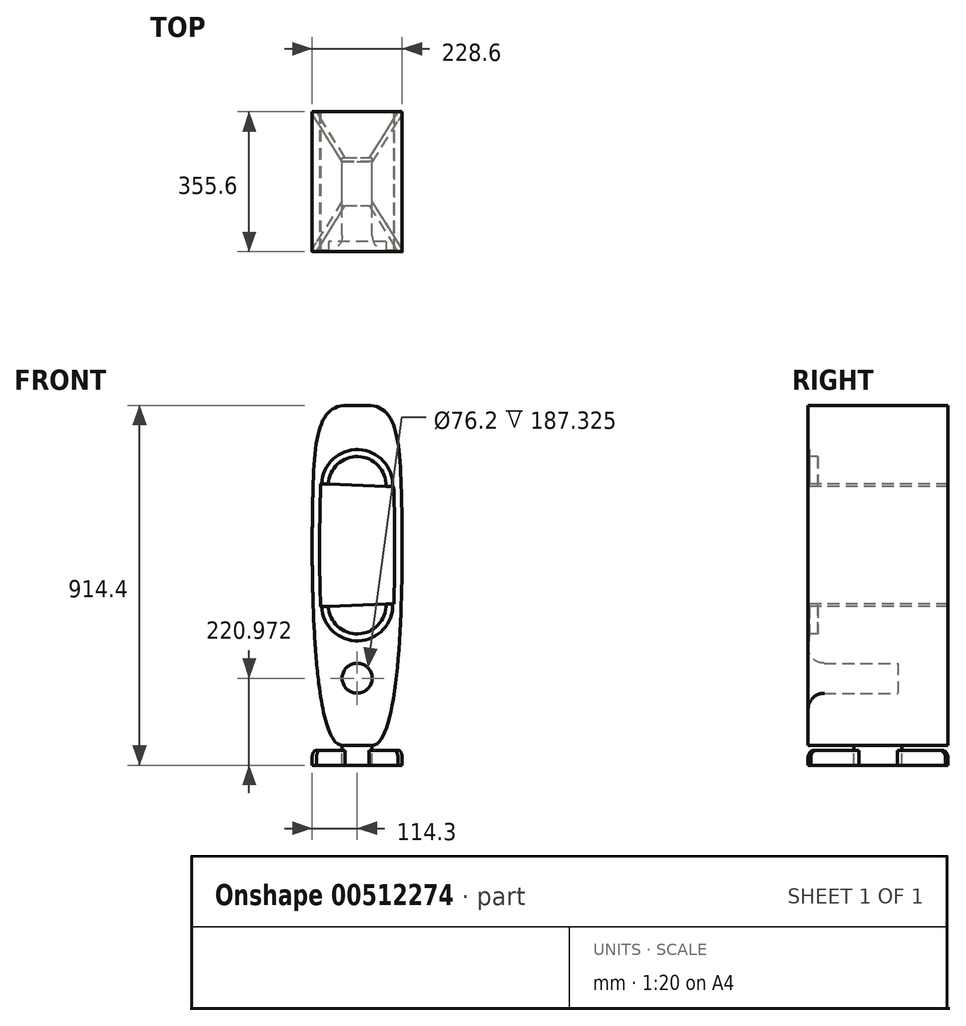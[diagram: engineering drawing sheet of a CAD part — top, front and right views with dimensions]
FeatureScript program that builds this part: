
annotation { "Feature Type Name" : "Feature", "Feature Type Description" : "" }
export const myFeature = defineFeature(function(context is Context, id is Id, definition is map)
    precondition{}
    {
        {
            var Q0;
            Q0=qCreatedBy(makeId("Front.planeOp"),FACE);
            var sketch = newSketch(context, id + "F0", { "sketchPlane" : qUnion([Q0])});
            skCircle(sketch, "E0", {"center": v(0, 152.4) * mm, "radius": 90.49 * mm});
            skCircle(sketch, "E1", {"center": v(0, 152.4) * mm, "radius": 73.03 * mm});
            skCircle(sketch, "E2", {"center": v(0, -152.4) * mm, "radius": 90.49 * mm});
            skCircle(sketch, "E3", {"center": v(0, -152.4) * mm, "radius": 73.03 * mm});
            skCircle(sketch, "E4", {"center": v(33.34, 0) * mm, "radius": 52.39 * mm});
            skCircle(sketch, "E5", {"center": v(33.34, 0) * mm, "radius": 38.1 * mm});
            skSolve(sketch);
        }
        {
            var Q0;
            Q0=qCreatedBy(makeId("Front.planeOp"),FACE);
            var sketch = newSketch(context, id + "F1", { "sketchPlane" : qUnion([Q0])});
            skLineSegment(sketch, "E6", {"start": v(-25.4, 355.6) * mm, "end": v(25.4, 355.6) * mm});
            skLineSegment(sketch, "E7", {"start": v(-38.1, -508) * mm, "end": v(38.1, -508) * mm});
            skFitSpline(sketch, "E8", {"points": [v(-25.4, 355.6) * mm, v(-112.46, 131.94) * mm, v(-38.1, -508) * mm], "startDerivative": vector(-581.78, 0) * mm, "endDerivative": vector(351.6, 0) * mm});
            skFitSpline(sketch, "E9", {"points": [v(25.4, 355.6) * mm, v(112.46, 131.94) * mm, v(38.1, -508) * mm], "startDerivative": vector(581.78, 0) * mm, "endDerivative": vector(-351.6, 0) * mm});
            skLineSegment(sketch, "E10", {"start": v(-114.3, 34.49) * mm, "end": v(-114.3, -81.25) * mm});
            skLineSegment(sketch, "E11", {"start": v(-111.69, 156.4) * mm, "end": v(-119.91, -73.49) * mm});
            skLineSegment(sketch, "E12", {"start": v(-111.69, 156.4) * mm, "end": v(0, 152.4) * mm});
            skLineSegment(sketch, "E13", {"start": v(0, -152.4) * mm, "end": v(-111.69, -156.4) * mm});
            skLineSegment(sketch, "E14", {"start": v(-111.64, -157.68) * mm, "end": v(-111.69, -156.4) * mm});
            skLineSegment(sketch, "E15", {"start": v(0, 152.4) * mm, "end": v(4258.77, 0) * mm});
            skLineSegment(sketch, "E16", {"start": v(4258.77, 0) * mm, "end": v(0, -152.4) * mm});
            skCircle(sketch, "E17", {"center": v(0, -337.83) * mm, "radius": 79.38 * mm});
            skLineSegment(sketch, "E18", {"start": v(0, -337.83) * mm, "end": v(-97.66, -350.04) * mm});
            skLineSegment(sketch, "E19", {"start": v(-97.66, -350.04) * mm, "end": v(-163.56, 177.1) * mm});
            skCircle(sketch, "E20", {"center": v(0, -337.83) * mm, "radius": 38.1 * mm});
            skFitSpline(sketch, "E21.0", {"points": [v(25.4, 336.55) * mm, v(27.86, 336.55) * mm, v(32.48, 336.33) * mm, v(38.57, 335.4) * mm, v(43.91, 333.96) * mm, v(48.62, 332.05) * mm, v(52.86, 329.66) * mm, v(56.78, 326.73) * mm, v(60.49, 323.17) * mm, v(64.04, 318.87) * mm, v(67.45, 313.74) * mm, v(70.68, 307.73) * mm, v(73.71, 300.82) * mm, v(77.46, 290.41) * mm, v(81.54, 275.18) * mm, v(85.44, 253.53) * mm, v(88.41, 228.7) * mm, v(90.6, 200.8) * mm, v(92.19, 170) * mm, v(93.14, 141.98) * mm, v(93.78, 118.21) * mm, v(94.35, 93.64) * mm, v(94.9, 61.54) * mm, v(95.25, 21.27) * mm, v(95.29, -34.17) * mm, v(94.4, -105.65) * mm, v(92.04, -177.05) * mm, v(89.1, -232.35) * mm, v(86.35, -272.46) * mm, v(83, -310.75) * mm, v(79.04, -346.75) * mm, v(74.43, -380) * mm, v(69.16, -409.99) * mm, v(64.21, -431.83) * mm, v(59.96, -447.12) * mm, v(56.63, -457.4) * mm, v(53.22, -466.41) * mm, v(49.76, -474.04) * mm, v(46.36, -480.18) * mm, v(43.7, -483.94) * mm, v(41.84, -486.11) * mm, v(40.61, -487.33) * mm, v(39.6, -488.16) * mm, v(38.85, -488.65) * mm, v(38.39, -488.88) * mm, v(38.18, -488.94) * mm, v(38.14, -488.95) * mm, v(38.13, -488.95) * mm, v(38.1, -488.95) * mm]});
            skLineSegment(sketch, "E21.1", {"start": v(-25.4, 336.55) * mm, "end": v(25.4, 336.55) * mm});
            skFitSpline(sketch, "E21.2", {"points": [v(-25.4, 336.55) * mm, v(-27.86, 336.55) * mm, v(-32.48, 336.33) * mm, v(-38.57, 335.4) * mm, v(-43.91, 333.96) * mm, v(-48.62, 332.05) * mm, v(-52.86, 329.66) * mm, v(-56.78, 326.73) * mm, v(-60.49, 323.17) * mm, v(-64.04, 318.87) * mm, v(-67.45, 313.74) * mm, v(-70.68, 307.73) * mm, v(-73.71, 300.82) * mm, v(-77.46, 290.41) * mm, v(-81.54, 275.18) * mm, v(-85.44, 253.53) * mm, v(-88.41, 228.7) * mm, v(-90.6, 200.8) * mm, v(-92.19, 170) * mm, v(-93.14, 141.98) * mm, v(-93.78, 118.21) * mm, v(-94.35, 93.64) * mm, v(-94.9, 61.54) * mm, v(-95.25, 21.27) * mm, v(-95.29, -34.17) * mm, v(-94.4, -105.65) * mm, v(-92.04, -177.05) * mm, v(-89.1, -232.35) * mm, v(-86.35, -272.46) * mm, v(-83, -310.75) * mm, v(-79.04, -346.75) * mm, v(-74.43, -380) * mm, v(-69.16, -409.99) * mm, v(-64.21, -431.83) * mm, v(-59.96, -447.12) * mm, v(-56.63, -457.4) * mm, v(-53.22, -466.41) * mm, v(-49.76, -474.04) * mm, v(-46.36, -480.18) * mm, v(-43.7, -483.94) * mm, v(-41.84, -486.11) * mm, v(-40.61, -487.33) * mm, v(-39.6, -488.16) * mm, v(-38.85, -488.65) * mm, v(-38.39, -488.88) * mm, v(-38.18, -488.94) * mm, v(-38.14, -488.95) * mm, v(-38.13, -488.95) * mm, v(-38.1, -488.95) * mm]});
            skLineSegment(sketch, "E21.3", {"start": v(-38.1, -488.95) * mm, "end": v(38.1, -488.95) * mm});
            skPoint(sketch, "E22", {"position": v(0, -299.73) * mm});
            skPoint(sketch, "E23", {"position": v(0, -258.45) * mm});
            skLineSegment(sketch, "E24", {"start": v(-95, 47.62) * mm, "end": v(95, 47.62) * mm});
            skLineSegment(sketch, "E25", {"start": v(-94.77, 66.67) * mm, "end": v(94.77, 66.67) * mm});
            skLineSegment(sketch, "E26", {"start": v(-94.82, -66.67) * mm, "end": v(94.82, -66.67) * mm});
            skLineSegment(sketch, "E27", {"start": v(-95.04, -47.62) * mm, "end": v(95.04, -47.62) * mm});
            skLineSegment(sketch, "E28", {"start": v(253.42, 57.15) * mm, "end": v(318.07, 57.15) * mm});
            skLineSegment(sketch, "E29", {"start": v(253.7, 61.91) * mm, "end": v(300.48, 61.91) * mm});
            skLineSegment(sketch, "E30", {"start": v(255.73, 52.39) * mm, "end": v(319.23, 52.39) * mm});
            skLineSegment(sketch, "E31", {"start": v(259.21, -61.91) * mm, "end": v(326.14, -61.91) * mm});
            skLineSegment(sketch, "E32", {"start": v(240.79, -57.15) * mm, "end": v(315.43, -57.15) * mm});
            skLineSegment(sketch, "E33", {"start": v(242.27, -52.39) * mm, "end": v(300.37, -52.39) * mm});
            skLineSegment(sketch, "E34", {"start": v(-89.03, -231.78) * mm, "end": v(89.03, -231.78) * mm});
            skLineSegment(sketch, "E35", {"start": v(-87.8, -250.83) * mm, "end": v(87.8, -250.83) * mm});
            skLineSegment(sketch, "E36", {"start": v(-74.37, -379.1) * mm, "end": v(74.37, -379.1) * mm});
            skLineSegment(sketch, "E37", {"start": v(-71.17, -398.15) * mm, "end": v(71.17, -398.15) * mm});
            skLineSegment(sketch, "E38", {"start": v(-85.6, 250.83) * mm, "end": v(85.6, 250.83) * mm});
            skLineSegment(sketch, "E39", {"start": v(-87.92, 231.78) * mm, "end": v(87.92, 231.78) * mm});
            skPoint(sketch, "E40", {"position": v(-78.76, -347.67) * mm});
            skSolve(sketch);
        }
        {
            var Q0;
            Q0=qCreatedBy(makeId("Right.planeOp"),FACE);
            var sketch = newSketch(context, id + "F2", { "sketchPlane" : qUnion([Q0])});
            skLineSegment(sketch, "E41", {"start": v(-179.41, -337.83) * mm, "end": v(228.6, -337.83) * mm});
            skLineSegment(sketch, "E42", {"start": v(0, -337.83) * mm, "end": v(0, -258.45) * mm});
            skArc(sketch, "E43", {"start": v(0, -258.45) * mm, "mid": v(12.09, -287.64) * mm, "end": v(41.28, -299.73) * mm});
            skLineSegment(sketch, "E44", {"start": v(41.28, -299.73) * mm, "end": v(228.6, -299.73) * mm});
            skLineSegment(sketch, "E45", {"start": v(228.6, -299.73) * mm, "end": v(228.6, -337.83) * mm});
            skSolve(sketch);
        }
        {
            var Q0;
            {var subQ6=sQuery(id+"F1.wireOp",EDGE,"E6");Q0=makeQuery(id+"F1.imprint","IMPRINT",FACE,{"disambiguationData":[TD([[makeQuery(id+"F1.imprint","IMPRINT",EDGE,{"derivedFrom":subQ6}),-1.0]])]});}
            var Q1;
            {var subQ0=sQuery(id+"F1.wireOp",EDGE,"E21.1");Q1=makeQuery(id+"F1.imprint","IMPRINT",FACE,{"disambiguationData":[TD([[makeQuery(id+"F1.imprint","IMPRINT",EDGE,{"derivedFrom":subQ0}),-1.0]])]});}
            var Q2;
            {var subQ2=sQuery(id+"F1.wireOp",EDGE,"E15");var subQ4=sQuery(id+"F1.wireOp",EDGE,"E9");var subQ5=makeQuery(id+"F1.imprint","INTERSECT",VERTEX,{"derivedFrom":[subQ4,subQ2]});Q2=makeQuery(id+"F1.imprint","IMPRINT",FACE,{"disambiguationData":[TD([[makeQuery(id+"F1.imprint","IMPRINT",EDGE,{"disambiguationData":[TD([[subQ5,-1.0]])],"derivedFrom":subQ4}),-1.0]])]});}
            var Q3;
            {var subQ2=sQuery(id+"F1.wireOp",EDGE,"E12");var subQ4=sQuery(id+"F1.wireOp",EDGE,"E8");var subQ5=makeQuery(id+"F1.imprint","INTERSECT",VERTEX,{"derivedFrom":[subQ4,subQ2]});Q3=makeQuery(id+"F1.imprint","IMPRINT",FACE,{"disambiguationData":[TD([[makeQuery(id+"F1.imprint","IMPRINT",EDGE,{"disambiguationData":[TD([[subQ5,-1.0]])],"derivedFrom":subQ4}),1.0]])]});}
            var Q4;
            {var subQ0=sQuery(id+"F1.wireOp",EDGE,"E25");Q4=makeQuery(id+"F1.imprint","IMPRINT",FACE,{"disambiguationData":[TD([[makeQuery(id+"F1.imprint","IMPRINT",EDGE,{"derivedFrom":subQ0}),1.0]])]});}
            var Q5;
            {var subQ0=sQuery(id+"F1.wireOp",EDGE,"E24");Q5=makeQuery(id+"F1.imprint","IMPRINT",FACE,{"disambiguationData":[TD([[makeQuery(id+"F1.imprint","IMPRINT",EDGE,{"derivedFrom":subQ0}),1.0]])]});}
            var Q6;
            {var subQ0=sQuery(id+"F1.wireOp",EDGE,"E24");Q6=makeQuery(id+"F1.imprint","IMPRINT",FACE,{"disambiguationData":[TD([[makeQuery(id+"F1.imprint","IMPRINT",EDGE,{"derivedFrom":subQ0}),-1.0]])]});}
            var Q7;
            {var subQ0=sQuery(id+"F1.wireOp",EDGE,"E26");Q7=makeQuery(id+"F1.imprint","IMPRINT",FACE,{"disambiguationData":[TD([[makeQuery(id+"F1.imprint","IMPRINT",EDGE,{"derivedFrom":subQ0}),1.0]])]});}
            var Q8;
            {var subQ0=sQuery(id+"F1.wireOp",EDGE,"E26");Q8=makeQuery(id+"F1.imprint","IMPRINT",FACE,{"disambiguationData":[TD([[makeQuery(id+"F1.imprint","IMPRINT",EDGE,{"derivedFrom":subQ0}),-1.0]])]});}
            var Q9;
            Q9=makeQuery(id+"F1.imprint","IMPRINT",FACE,{"disambiguationData":[TD([[makeQuery(id+"F1.imprint","IMPRINT",EDGE,{"derivedFrom":sQuery(id+"F1.wireOp",EDGE,"E17")}),-1.0]])]});
            var Q10;
            {var subQ6=sQuery(id+"F1.wireOp",EDGE,"E7");Q10=makeQuery(id+"F1.imprint","IMPRINT",FACE,{"disambiguationData":[TD([[makeQuery(id+"F1.imprint","IMPRINT",EDGE,{"derivedFrom":subQ6}),1.0]])]});}
            var Q11;
            Q11=makeQuery(id+"F1.imprint","IMPRINT",FACE,{"disambiguationData":[TD([[makeQuery(id+"F1.imprint","IMPRINT",EDGE,{"derivedFrom":sQuery(id+"F1.wireOp",EDGE,"E17")}),1.0]])]});
            var Q12;
            {var subQ0=sQuery(id+"F1.wireOp",EDGE,"E13");var subQ1=sQuery(id+"F1.wireOp",EDGE,"E8");var subQ2=makeQuery(id+"F1.imprint","INTERSECT",VERTEX,{"derivedFrom":[subQ1,subQ0]});Q12=makeQuery(id+"F1.imprint","IMPRINT",FACE,{"disambiguationData":[TD([[makeQuery(id+"F1.imprint","IMPRINT",EDGE,{"disambiguationData":[TD([[subQ2,-1.0]])],"derivedFrom":subQ1}),1.0]])]});}
            var Q13;
            Q13=makeQuery(id+"F1.imprint","IMPRINT",FACE,{"disambiguationData":[TD([[makeQuery(id+"F1.imprint","IMPRINT",EDGE,{"derivedFrom":sQuery(id+"F1.wireOp",EDGE,"E20")}),1.0]])]});
            var Q14;
            {var subQ0=sQuery(id+"F1.wireOp",EDGE,"E39");Q14=makeQuery(id+"F1.imprint","IMPRINT",FACE,{"disambiguationData":[TD([[makeQuery(id+"F1.imprint","IMPRINT",EDGE,{"derivedFrom":subQ0}),-1.0]])]});}
            var Q15;
            {var subQ0=sQuery(id+"F1.wireOp",EDGE,"E38");Q15=makeQuery(id+"F1.imprint","IMPRINT",FACE,{"disambiguationData":[TD([[makeQuery(id+"F1.imprint","IMPRINT",EDGE,{"derivedFrom":subQ0}),-1.0]])]});}
            var Q16;
            {var subQ0=sQuery(id+"F1.wireOp",EDGE,"E34");Q16=makeQuery(id+"F1.imprint","IMPRINT",FACE,{"disambiguationData":[TD([[makeQuery(id+"F1.imprint","IMPRINT",EDGE,{"derivedFrom":subQ0}),1.0]])]});}
            var Q17;
            {var subQ0=sQuery(id+"F1.wireOp",EDGE,"E34");Q17=makeQuery(id+"F1.imprint","IMPRINT",FACE,{"disambiguationData":[TD([[makeQuery(id+"F1.imprint","IMPRINT",EDGE,{"derivedFrom":subQ0}),-1.0]])]});}
            var Q18;
            {var subQ0=sQuery(id+"F1.wireOp",EDGE,"E35");Q18=makeQuery(id+"F1.imprint","IMPRINT",FACE,{"disambiguationData":[TD([[makeQuery(id+"F1.imprint","IMPRINT",EDGE,{"derivedFrom":subQ0}),-1.0]])]});}
            var Q19;
            {var subQ0=sQuery(id+"F1.wireOp",EDGE,"E21.3");Q19=makeQuery(id+"F1.imprint","IMPRINT",FACE,{"disambiguationData":[TD([[makeQuery(id+"F1.imprint","IMPRINT",EDGE,{"derivedFrom":subQ0}),1.0]])]});}
            var Q20;
            {var subQ0=sQuery(id+"F1.wireOp",EDGE,"E36");var subQ1=sQuery(id+"F1.wireOp",EDGE,"E17");var subQ2=makeQuery(id+"F1.imprint","INTERSECT",VERTEX,{"disambiguationData":[OD(0.0)],"derivedFrom":[subQ1,subQ0]});Q20=makeQuery(id+"F1.imprint","IMPRINT",FACE,{"disambiguationData":[TD([[makeQuery(id+"F1.imprint","IMPRINT",EDGE,{"disambiguationData":[TD([[subQ2,-1.0]])],"derivedFrom":subQ1}),1.0]])]});}
            var Q21;
            {var subQ0=sQuery(id+"F1.wireOp",EDGE,"E36");var subQ3=sQuery(id+"F1.wireOp",EDGE,"E17");var subQ4=makeQuery(id+"F1.imprint","INTERSECT",VERTEX,{"disambiguationData":[OD(0.0)],"derivedFrom":[subQ3,subQ0]});Q21=makeQuery(id+"F1.imprint","IMPRINT",FACE,{"disambiguationData":[TD([[makeQuery(id+"F1.imprint","IMPRINT",EDGE,{"disambiguationData":[TD([[subQ4,-1.0]])],"derivedFrom":subQ3}),-1.0]])]});}
            var Q22;
            {var subQ0=sQuery(id+"F1.wireOp",EDGE,"E37");var subQ1=sQuery(id+"F1.wireOp",EDGE,"E17");var subQ2=makeQuery(id+"F1.imprint","INTERSECT",VERTEX,{"disambiguationData":[OD(0.0)],"derivedFrom":[subQ1,subQ0]});Q22=makeQuery(id+"F1.imprint","IMPRINT",FACE,{"disambiguationData":[TD([[makeQuery(id+"F1.imprint","IMPRINT",EDGE,{"disambiguationData":[TD([[subQ2,-1.0]])],"derivedFrom":subQ1}),1.0]])]});}
            var Q23;
            {var subQ0=sQuery(id+"F1.wireOp",EDGE,"E37");var subQ1=sQuery(id+"F1.wireOp",EDGE,"E17");var subQ2=makeQuery(id+"F1.imprint","INTERSECT",VERTEX,{"disambiguationData":[OD(1.0)],"derivedFrom":[subQ1,subQ0]});Q23=makeQuery(id+"F1.imprint","IMPRINT",FACE,{"disambiguationData":[TD([[makeQuery(id+"F1.imprint","IMPRINT",EDGE,{"disambiguationData":[TD([[subQ2,-1.0]])],"derivedFrom":subQ1}),-1.0]])]});}
            extrude(context, id + "F3", {"entities" : qUnion([Q0, Q1, Q2, Q3, Q4, Q5, Q6, Q7, Q8, Q9, Q10, Q11, Q12, Q13, Q14, Q15, Q16, Q17, Q18, Q19, Q20, Q21, Q22, Q23]), "oppositeDirection" : true, "depth" : 355.6 * mm});
        }
        {
            var Q0;
            Q0=makeQuery(id+"F0.imprint","IMPRINT",FACE,{"disambiguationData":[TD([[makeQuery(id+"F0.imprint","IMPRINT",EDGE,{"derivedFrom":sQuery(id+"F0.wireOp",EDGE,"E0")}),1.0]])]});
            var Q1;
            Q1=makeQuery(id+"F0.imprint","IMPRINT",FACE,{"disambiguationData":[TD([[makeQuery(id+"F0.imprint","IMPRINT",EDGE,{"derivedFrom":sQuery(id+"F0.wireOp",EDGE,"E4")}),1.0]])]});
            var Q2;
            Q2=makeQuery(id+"F0.imprint","IMPRINT",FACE,{"disambiguationData":[TD([[makeQuery(id+"F0.imprint","IMPRINT",EDGE,{"derivedFrom":sQuery(id+"F0.wireOp",EDGE,"E2")}),1.0]])]});
            extrude(context, id + "F4", {"entities" : qUnion([Q0, Q1, Q2]), "operationType" : NewBodyOperationType.REMOVE, "oppositeDirection" : true, "depth" : 3.17 * mm});
        }
        {
            var Q0;
            Q0=makeQuery(id+"F0.imprint","IMPRINT",FACE,{"disambiguationData":[TD([[makeQuery(id+"F0.imprint","IMPRINT",EDGE,{"derivedFrom":sQuery(id+"F0.wireOp",EDGE,"E1")}),1.0]])]});
            var Q1;
            Q1=makeQuery(id+"F0.imprint","IMPRINT",FACE,{"disambiguationData":[TD([[makeQuery(id+"F0.imprint","IMPRINT",EDGE,{"derivedFrom":sQuery(id+"F0.wireOp",EDGE,"E5")}),1.0]])]});
            var Q2;
            Q2=makeQuery(id+"F0.imprint","IMPRINT",FACE,{"disambiguationData":[TD([[makeQuery(id+"F0.imprint","IMPRINT",EDGE,{"derivedFrom":sQuery(id+"F0.wireOp",EDGE,"E3")}),1.0]])]});
            extrude(context, id + "F5", {"entities" : qUnion([Q0, Q1, Q2]), "operationType" : NewBodyOperationType.REMOVE, "oppositeDirection" : true, "depth" : 25.4 * mm});
        }
        {
            var Q0;
            Q0=qSketchRegion(id+"F2",true);
            var Q1;
            Q1=sQuery(id+"F2.wireOp",EDGE,"E41");
            revolve(context, id + "F6", {"operationType" : NewBodyOperationType.REMOVE, "entities" : qUnion([Q0]), "axis" : qUnion([Q1]), "revolveType" : RevolveType.FULL, "oppositeDirection" : true});
        }
        {
            var Q0;
            Q0=makeQuery(id+"F3.opExtrude","CAP_EDGE",EDGE,{"disambiguationData":[OSD([sQuery(id+"F1.wireOp",EDGE,"E7")])],"isStart":true});
            cPoint(context, id + "F7", {"entities" : qUnion([Q0]), "parameter" : 0.5});
        }
        {
            var Q0;
            Q0=qCreatedBy(makeId("Top.planeOp"),FACE);
            var Q1;
            Q1=qCreatedBy(id+"F7",VERTEX);
            cPlane(context, id + "F8", {"entities" : qUnion([Q0, Q1]), "cplaneType" : CPlaneType.PLANE_POINT, "offset" : 25.4 * mm, "width" : 152.4 * mm, "height" : 152.4 * mm});
        }
        {
            var Q0;
            Q0=qCreatedBy(id+"F8.planeOp",FACE);
            var sketch = newSketch(context, id + "F9", { "sketchPlane" : qUnion([Q0])});
            skLineSegment(sketch, "E46.bottom", {"start": v(-114.3, 0) * mm, "end": v(114.3, 0) * mm});
            skLineSegment(sketch, "E46.top", {"start": v(-114.3, 355.6) * mm, "end": v(114.3, 355.6) * mm});
            skLineSegment(sketch, "E46.left", {"start": v(-114.3, 0) * mm, "end": v(-114.3, 355.6) * mm});
            skLineSegment(sketch, "E46.right", {"start": v(114.3, 0) * mm, "end": v(114.3, 355.6) * mm});
            skLineSegment(sketch, "E47.bottom", {"start": v(-38.1, 116.78) * mm, "end": v(38.1, 116.78) * mm});
            skLineSegment(sketch, "E47.top", {"start": v(-38.1, 238.82) * mm, "end": v(38.1, 238.82) * mm});
            skLineSegment(sketch, "E47.left", {"start": v(-38.1, 116.78) * mm, "end": v(-38.1, 238.82) * mm});
            skLineSegment(sketch, "E47.right", {"start": v(38.1, 116.78) * mm, "end": v(38.1, 238.82) * mm});
            skLineSegment(sketch, "E48", {"start": v(-114.3, 6.73) * mm, "end": v(-103.53, 0) * mm});
            skLineSegment(sketch, "E49", {"start": v(-103.53, 0) * mm, "end": v(0, 165.81) * mm});
            skLineSegment(sketch, "E50", {"start": v(0, 165.81) * mm, "end": v(103.53, 0) * mm});
            skLineSegment(sketch, "E51", {"start": v(103.53, 0) * mm, "end": v(114.3, 6.73) * mm});
            skLineSegment(sketch, "E52", {"start": v(114.3, 6.73) * mm, "end": v(7.49, 177.8) * mm});
            skLineSegment(sketch, "E53", {"start": v(7.49, 177.8) * mm, "end": v(114.3, 348.87) * mm});
            skLineSegment(sketch, "E54", {"start": v(114.3, 348.87) * mm, "end": v(103.53, 355.6) * mm});
            skLineSegment(sketch, "E55", {"start": v(103.53, 355.6) * mm, "end": v(0, 189.79) * mm});
            skLineSegment(sketch, "E56", {"start": v(0, 189.79) * mm, "end": v(-103.53, 355.6) * mm});
            skLineSegment(sketch, "E57", {"start": v(-103.53, 355.6) * mm, "end": v(-114.3, 348.87) * mm});
            skLineSegment(sketch, "E58", {"start": v(-114.3, 348.87) * mm, "end": v(-7.49, 177.8) * mm});
            skLineSegment(sketch, "E59", {"start": v(-7.49, 177.8) * mm, "end": v(-114.3, 6.73) * mm});
            skLineSegment(sketch, "E60", {"start": v(16.66, 151.12) * mm, "end": v(60.9, 80.27) * mm});
            skPoint(sketch, "E60.endSnap0", {"position": v(60.9, 92.26) * mm});
            skSolve(sketch);
        }
        {
            var Q0;
            {var subQ0=sQuery(id+"F9.wireOp",EDGE,"E52");var subQ1=sQuery(id+"F9.wireOp",EDGE,"E47.right");var subQ2=makeQuery(id+"F9.imprint","INTERSECT",VERTEX,{"derivedFrom":[subQ1,subQ0]});Q0=makeQuery(id+"F9.imprint","IMPRINT",FACE,{"disambiguationData":[TD([[makeQuery(id+"F9.imprint","IMPRINT",EDGE,{"disambiguationData":[TD([[subQ2,-1.0]])],"derivedFrom":subQ1}),1.0]])]});}
            var Q1;
            {var subQ0=sQuery(id+"F9.wireOp",EDGE,"E49");var subQ1=sQuery(id+"F9.wireOp",EDGE,"E47.bottom");var subQ2=makeQuery(id+"F9.imprint","INTERSECT",VERTEX,{"derivedFrom":[subQ1,subQ0]});Q1=makeQuery(id+"F9.imprint","IMPRINT",FACE,{"disambiguationData":[TD([[makeQuery(id+"F9.imprint","IMPRINT",EDGE,{"disambiguationData":[TD([[subQ2,-1.0]])],"derivedFrom":subQ1}),1.0]])]});}
            var Q2;
            {var subQ0=sQuery(id+"F9.wireOp",EDGE,"E59");var subQ1=sQuery(id+"F9.wireOp",EDGE,"E47.left");var subQ2=makeQuery(id+"F9.imprint","INTERSECT",VERTEX,{"derivedFrom":[subQ1,subQ0]});Q2=makeQuery(id+"F9.imprint","IMPRINT",FACE,{"disambiguationData":[TD([[makeQuery(id+"F9.imprint","IMPRINT",EDGE,{"disambiguationData":[TD([[subQ2,-1.0]])],"derivedFrom":subQ1}),-1.0]])]});}
            var Q3;
            {var subQ0=sQuery(id+"F9.wireOp",EDGE,"E56");var subQ1=sQuery(id+"F9.wireOp",EDGE,"E47.top");var subQ2=makeQuery(id+"F9.imprint","INTERSECT",VERTEX,{"derivedFrom":[subQ1,subQ0]});Q3=makeQuery(id+"F9.imprint","IMPRINT",FACE,{"disambiguationData":[TD([[makeQuery(id+"F9.imprint","IMPRINT",EDGE,{"disambiguationData":[TD([[subQ2,-1.0]])],"derivedFrom":subQ1}),-1.0]])]});}
            var Q4;
            {var subQ3=sQuery(id+"F9.wireOp",EDGE,"E47.bottom");var subQ9=sQuery(id+"F9.wireOp",EDGE,"E47.left");var subQ14=makeQuery(id+"F9.imprint","INTERSECT",VERTEX,{"derivedFrom":[subQ3,subQ9]});Q4=makeQuery(id+"F9.imprint","IMPRINT",FACE,{"disambiguationData":[TD([[makeQuery(id+"F9.imprint","IMPRINT",EDGE,{"disambiguationData":[TD([[subQ14,-1.0]])],"derivedFrom":subQ3}),1.0]])]});}
            extrude(context, id + "F10", {"entities" : qUnion([Q0, Q1, Q2, Q3, Q4]), "operationType" : NewBodyOperationType.ADD, "oppositeDirection" : true, "depth" : 50.8 * mm});
        }
        {
            var Q0;
            {var subQ1=sQuery(id+"F9.wireOp",EDGE,"E48");Q0=makeQuery(id+"F9.imprint","IMPRINT",FACE,{"disambiguationData":[TD([[makeQuery(id+"F9.imprint","IMPRINT",EDGE,{"derivedFrom":subQ1}),1.0]])]});}
            var Q1;
            {var subQ0=sQuery(id+"F9.wireOp",EDGE,"E51");Q1=makeQuery(id+"F9.imprint","IMPRINT",FACE,{"disambiguationData":[TD([[makeQuery(id+"F9.imprint","IMPRINT",EDGE,{"derivedFrom":subQ0}),1.0]])]});}
            var Q2;
            {var subQ0=sQuery(id+"F9.wireOp",EDGE,"E54");Q2=makeQuery(id+"F9.imprint","IMPRINT",FACE,{"disambiguationData":[TD([[makeQuery(id+"F9.imprint","IMPRINT",EDGE,{"derivedFrom":subQ0}),1.0]])]});}
            var Q3;
            {var subQ0=sQuery(id+"F9.wireOp",EDGE,"E57");Q3=makeQuery(id+"F9.imprint","IMPRINT",FACE,{"disambiguationData":[TD([[makeQuery(id+"F9.imprint","IMPRINT",EDGE,{"derivedFrom":subQ0}),1.0]])]});}
            extrude(context, id + "F11", {"entities" : qUnion([Q0, Q1, Q2, Q3]), "operationType" : NewBodyOperationType.ADD, "oppositeDirection" : true, "depth" : 50.8 * mm, "hasSecondDirection" : true, "secondDirectionOppositeDirection" : false, "secondDirectionDepth" : -12.7 * mm});
        }
        {
            var Q0;
            Q0=makeQuery(id+"F11.opExtrude","CAP_EDGE",EDGE,{"disambiguationData":[OSD([sQuery(id+"F9.wireOp",EDGE,"E48")])],"isStart":true});
            var Q1;
            Q1=makeQuery(id+"F11.opExtrude","CAP_EDGE",EDGE,{"disambiguationData":[OSD([sQuery(id+"F9.wireOp",EDGE,"E54")])],"isStart":true});
            var Q2;
            Q2=makeQuery(id+"F11.opExtrude","CAP_EDGE",EDGE,{"disambiguationData":[OSD([sQuery(id+"F9.wireOp",EDGE,"E51")])],"isStart":true});
            var Q3;
            Q3=makeQuery(id+"F11.opExtrude","CAP_EDGE",EDGE,{"disambiguationData":[OSD([sQuery(id+"F9.wireOp",EDGE,"E57")])],"isStart":true});
            fillet(context, id + "F12", {"entities" : qUnion([Q0, Q1, Q2, Q3]), "radius" : 19.05 * mm, "tangentPropagation" : true, "allowEdgeOverflow" : false});
        }
    });
